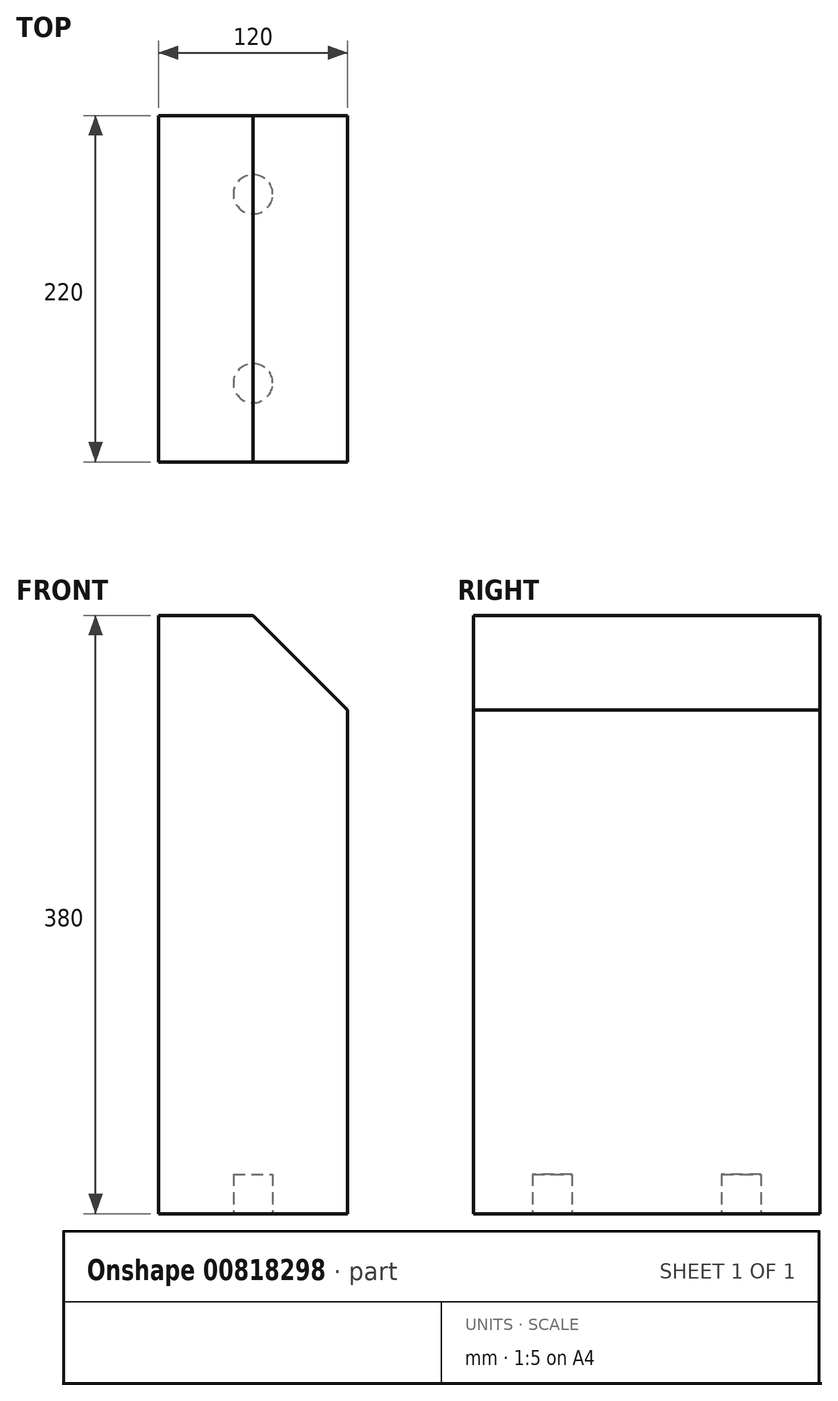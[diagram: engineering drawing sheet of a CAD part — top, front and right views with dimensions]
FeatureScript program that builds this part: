
annotation { "Feature Type Name" : "Feature", "Feature Type Description" : "" }
export const myFeature = defineFeature(function(context is Context, id is Id, definition is map)
    precondition{}
    {
        {
            var Q0;
            Q0=qCreatedBy(makeId("Right.planeOp"),FACE);
            var sketch = newSketch(context, id + "F0", { "sketchPlane" : qUnion([Q0])});
            skLineSegment(sketch, "E0.bottom", {"start": v(-110, 190) * mm, "end": v(110, 190) * mm});
            skLineSegment(sketch, "E0.top", {"start": v(-110, -190) * mm, "end": v(110, -190) * mm});
            skLineSegment(sketch, "E0.left", {"start": v(-110, 190) * mm, "end": v(-110, -190) * mm});
            skLineSegment(sketch, "E0.right", {"start": v(110, 190) * mm, "end": v(110, -190) * mm});
            skPoint(sketch, "E0.middle", {"position": v(0, 0) * mm});
            skSolve(sketch);
        }
        {
            var Q0;
            Q0 = qSketchRegion(id + "F0", true);
            extrude(context, id + "F1", {"entities" : qUnion([Q0]), "oppositeDirection" : true, "depth" : 120 * mm, "offsetDistance" : 25 * mm});
        }
        {
            var Q0;
            Q0=makeQuery(id+"F1.opExtrude","SWEPT_FACE",FACE,{"disambiguationData":[OSD([sQuery(id+"F0.wireOp",EDGE,"E0.left")])]});
            var sketch = newSketch(context, id + "F2", { "sketchPlane" : qUnion([Q0])});
            skLineSegment(sketch, "E1", {"start": v(-60, 190) * mm, "end": v(0, 130) * mm});
            skLineSegment(sketch, "E2", {"start": v(0, 130) * mm, "end": v(0, 190) * mm});
            skLineSegment(sketch, "E3", {"start": v(0, 190) * mm, "end": v(-60, 190) * mm});
            skSolve(sketch);
        }
        {
            var Q0;
            Q0 = qSketchRegion(id + "F2", true);
            extrude(context, id + "F3", {"entities" : qUnion([Q0]), "operationType" : NewBodyOperationType.REMOVE, "oppositeDirection" : true, "depth" : 220 * mm, "offsetDistance" : 25 * mm});
        }
        {
            var Q0;
            Q0=makeQuery(id+"F1.opExtrude","SWEPT_FACE",FACE,{"disambiguationData":[OSD([sQuery(id+"F0.wireOp",EDGE,"E0.top")])]});
            var sketch = newSketch(context, id + "F4", { "sketchPlane" : qUnion([Q0])});
            skLineSegment(sketch, "E4.0.0", {"start": v(0, -110) * mm, "end": v(0, 110) * mm, "construction": true});
            skLineSegment(sketch, "E4.0.1", {"start": v(0, 110) * mm, "end": v(-120, 110) * mm, "construction": true});
            skLineSegment(sketch, "E4.0.2", {"start": v(-120, 110) * mm, "end": v(-120, -110) * mm, "construction": true});
            skLineSegment(sketch, "E4.0.3", {"start": v(-120, -110) * mm, "end": v(0, -110) * mm, "construction": true});
            skCircle(sketch, "E5", {"center": v(-60, 60) * mm, "radius": 12.5 * mm});
            skPoint(sketch, "E5.centerSnap0", {"position": v(-60, 110) * mm});
            skCircle(sketch, "E6", {"center": v(-60, -60) * mm, "radius": 12.5 * mm});
            skPoint(sketch, "E6.centerSnap0", {"position": v(-60, -110) * mm});
            skSolve(sketch);
        }
        {
            var Q0;
            Q0 = qSketchRegion(id + "F4", true);
            extrude(context, id + "F5", {"entities" : qUnion([Q0]), "operationType" : NewBodyOperationType.REMOVE, "oppositeDirection" : true, "depth" : 25 * mm, "offsetDistance" : 25 * mm});
        }
    });
